# Revit family: Amicus
name_source: partatom
category: Mechanical Equipment
revit_build: Autodesk Revit 2018 (Build: 20190510_1515(x64)
units: mm (PartAtom-declared; Revit-internal decimal feet)

## family parameters
Always vertical = Yes
Cut with Voids When Loaded = No
OmniClass Number = 23.75.00.00
OmniClass Title = Climate Control (HVAC)
Part Type = Normal
Room Calculation Point = No
Round Connector Dimension = Use Diameter
Shared = No
Work Plane-Based = No

## types (4) — shared parameters
Manufacturer = Masterwatt B.V.
Materiaal 1 = Kunststof wit
Materiaal 2 = Kunststof licht grijs mat
URL = https://masterwatt.nl
Volt = 230 V

## per-type parameters (varying)
| type | Art. No. | Watt |
| Amicus 3 | 200 360 035 | 3500 VA |
| Amicus 4 | 200 360 044 | 4400 VA |
| Amicus 5 | 200 360 055 | 5500 VA |
| Amicus 6 | 200 360 060 | 6000 VA |

note: column(s) folded — value = type name in every type: Model

## geometry (parser evidence)
native form markers: Sweep x2
no freeform markers — native parametric forms only
